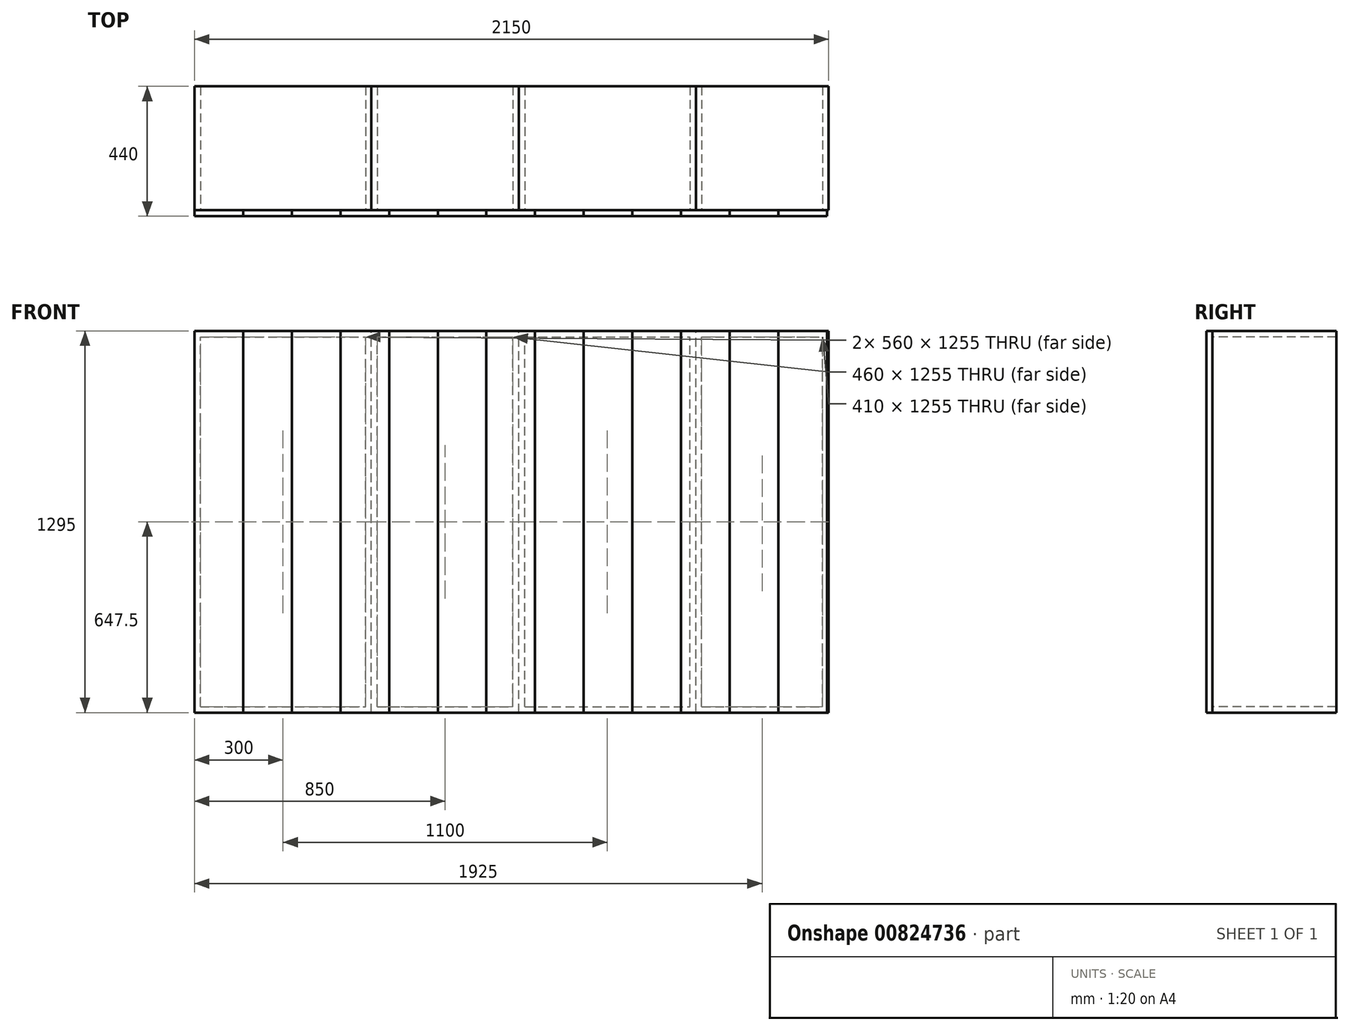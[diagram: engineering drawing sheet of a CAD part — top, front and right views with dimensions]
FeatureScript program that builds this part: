
annotation { "Feature Type Name" : "Feature", "Feature Type Description" : "" }
export const myFeature = defineFeature(function(context is Context, id is Id, definition is map)
    precondition{}
    {
        {
            var Q0;
            Q0=qCreatedBy(makeId("Front.planeOp"),FACE);
            var sketch = newSketch(context, id + "F0", { "sketchPlane" : qUnion([Q0])});
            skLineSegment(sketch, "E0.bottom", {"start": v(0, 0) * mm, "end": v(600, 0) * mm});
            skLineSegment(sketch, "E0.top", {"start": v(0, 1295) * mm, "end": v(600, 1295) * mm});
            skLineSegment(sketch, "E0.left", {"start": v(0, 0) * mm, "end": v(0, 1295) * mm});
            skLineSegment(sketch, "E0.right", {"start": v(600, 0) * mm, "end": v(600, 1295) * mm});
            skLineSegment(sketch, "E1.0", {"start": v(20, 1275) * mm, "end": v(580, 1275) * mm});
            skLineSegment(sketch, "E1.1", {"start": v(20, 20) * mm, "end": v(20, 1275) * mm});
            skLineSegment(sketch, "E1.2", {"start": v(20, 20) * mm, "end": v(580, 20) * mm});
            skLineSegment(sketch, "E1.3", {"start": v(580, 20) * mm, "end": v(580, 1275) * mm});
            skSolve(sketch);
        }
        {
            var Q0;
            Q0 = qSketchRegion(id + "F0", true);
            extrude(context, id + "F1", {"entities" : qUnion([Q0]), "oppositeDirection" : true, "depth" : 420 * mm, "offsetDistance" : 25 * mm});
        }
        {
            var Q0;
            Q0=makeQuery(id+"F1.opExtrude","CAP_FACE",FACE,{"disambiguationData":[OSD([sQuery(id+"F0.wireOp",EDGE,"E0.bottom"),sQuery(id+"F0.wireOp",EDGE,"E0.top"),sQuery(id+"F0.wireOp",EDGE,"E0.left"),sQuery(id+"F0.wireOp",EDGE,"E0.right"),sQuery(id+"F0.wireOp",EDGE,"E1.0"),sQuery(id+"F0.wireOp",EDGE,"E1.1"),sQuery(id+"F0.wireOp",EDGE,"E1.2"),sQuery(id+"F0.wireOp",EDGE,"E1.3")])],"isStart":true});
            var sketch = newSketch(context, id + "F2", { "sketchPlane" : qUnion([Q0])});
            skLineSegment(sketch, "E2.bottom", {"start": v(600, 0) * mm, "end": v(1100, 0) * mm});
            skLineSegment(sketch, "E2.top", {"start": v(600, 1295) * mm, "end": v(1100, 1295) * mm});
            skLineSegment(sketch, "E2.left", {"start": v(600, 0) * mm, "end": v(600, 1295) * mm});
            skLineSegment(sketch, "E2.right", {"start": v(1100, 0) * mm, "end": v(1100, 1295) * mm});
            skLineSegment(sketch, "E3.0", {"start": v(620, 20) * mm, "end": v(620, 1275) * mm});
            skLineSegment(sketch, "E3.1", {"start": v(620, 20) * mm, "end": v(1080, 20) * mm});
            skLineSegment(sketch, "E3.2", {"start": v(1080, 20) * mm, "end": v(1080, 1275) * mm});
            skLineSegment(sketch, "E3.3", {"start": v(620, 1275) * mm, "end": v(1080, 1275) * mm});
            skSolve(sketch);
        }
        {
            var Q0;
            Q0 = qSketchRegion(id + "F2", true);
            extrude(context, id + "F3", {"entities" : qUnion([Q0]), "oppositeDirection" : true, "depth" : 420 * mm, "offsetDistance" : 25 * mm});
        }
        {
            var Q0;
            Q0=makeQuery(id+"F3.opExtrude","CAP_FACE",FACE,{"disambiguationData":[OSD([sQuery(id+"F2.wireOp",EDGE,"E2.bottom"),sQuery(id+"F2.wireOp",EDGE,"E2.top"),sQuery(id+"F2.wireOp",EDGE,"E2.left"),sQuery(id+"F2.wireOp",EDGE,"E2.right"),sQuery(id+"F2.wireOp",EDGE,"E3.0"),sQuery(id+"F2.wireOp",EDGE,"E3.1"),sQuery(id+"F2.wireOp",EDGE,"E3.2"),sQuery(id+"F2.wireOp",EDGE,"E3.3")])],"isStart":true});
            var sketch = newSketch(context, id + "F4", { "sketchPlane" : qUnion([Q0])});
            skLineSegment(sketch, "E4.bottom", {"start": v(1100, 0) * mm, "end": v(1700, 0) * mm});
            skLineSegment(sketch, "E4.top", {"start": v(1100, 1295) * mm, "end": v(1700, 1295) * mm});
            skLineSegment(sketch, "E4.left", {"start": v(1100, 0) * mm, "end": v(1100, 1295) * mm});
            skLineSegment(sketch, "E4.right", {"start": v(1700, 0) * mm, "end": v(1700, 1295) * mm});
            skLineSegment(sketch, "E5.0", {"start": v(1120, 20) * mm, "end": v(1120, 1275) * mm});
            skLineSegment(sketch, "E5.1", {"start": v(1120, 20) * mm, "end": v(1680, 20) * mm});
            skLineSegment(sketch, "E5.2", {"start": v(1680, 20) * mm, "end": v(1680, 1275) * mm});
            skLineSegment(sketch, "E5.3", {"start": v(1120, 1275) * mm, "end": v(1680, 1275) * mm});
            skSolve(sketch);
        }
        {
            var Q0;
            Q0 = qSketchRegion(id + "F4", true);
            extrude(context, id + "F5", {"entities" : qUnion([Q0]), "oppositeDirection" : true, "depth" : 420 * mm, "offsetDistance" : 25 * mm});
        }
        {
            var Q0;
            Q0=makeQuery(id+"F5.opExtrude","CAP_FACE",FACE,{"disambiguationData":[OSD([sQuery(id+"F4.wireOp",EDGE,"E4.bottom"),sQuery(id+"F4.wireOp",EDGE,"E4.top"),sQuery(id+"F4.wireOp",EDGE,"E4.left"),sQuery(id+"F4.wireOp",EDGE,"E4.right"),sQuery(id+"F4.wireOp",EDGE,"E5.0"),sQuery(id+"F4.wireOp",EDGE,"E5.1"),sQuery(id+"F4.wireOp",EDGE,"E5.2"),sQuery(id+"F4.wireOp",EDGE,"E5.3")])],"isStart":true});
            var sketch = newSketch(context, id + "F6", { "sketchPlane" : qUnion([Q0])});
            skLineSegment(sketch, "E6.bottom", {"start": v(1700, 0) * mm, "end": v(2150, 0) * mm});
            skLineSegment(sketch, "E6.top", {"start": v(1700, 1295) * mm, "end": v(2150, 1295) * mm});
            skLineSegment(sketch, "E6.left", {"start": v(1700, 0) * mm, "end": v(1700, 1295) * mm});
            skLineSegment(sketch, "E6.right", {"start": v(2150, 0) * mm, "end": v(2150, 1295) * mm});
            skLineSegment(sketch, "E7.0", {"start": v(1720, 20) * mm, "end": v(1720, 1275) * mm});
            skLineSegment(sketch, "E7.1", {"start": v(1720, 20) * mm, "end": v(2130, 20) * mm});
            skLineSegment(sketch, "E7.2", {"start": v(2130, 20) * mm, "end": v(2130, 1275) * mm});
            skLineSegment(sketch, "E7.3", {"start": v(1720, 1275) * mm, "end": v(2130, 1275) * mm});
            skSolve(sketch);
        }
        {
            var Q0;
            Q0 = qSketchRegion(id + "F6", true);
            extrude(context, id + "F7", {"entities" : qUnion([Q0]), "oppositeDirection" : true, "depth" : 420 * mm, "offsetDistance" : 25 * mm});
        }
        {
            var Q0;
            Q0=makeQuery(id+"F1.opExtrude","CAP_FACE",FACE,{"disambiguationData":[OSD([sQuery(id+"F0.wireOp",EDGE,"E0.bottom"),sQuery(id+"F0.wireOp",EDGE,"E0.top"),sQuery(id+"F0.wireOp",EDGE,"E0.left"),sQuery(id+"F0.wireOp",EDGE,"E0.right"),sQuery(id+"F0.wireOp",EDGE,"E1.0"),sQuery(id+"F0.wireOp",EDGE,"E1.1"),sQuery(id+"F0.wireOp",EDGE,"E1.2"),sQuery(id+"F0.wireOp",EDGE,"E1.3")])],"isStart":true});
            var sketch = newSketch(context, id + "F8", { "sketchPlane" : qUnion([Q0])});
            skLineSegment(sketch, "E8.bottom", {"start": v(0, 0) * mm, "end": v(165, 0) * mm});
            skLineSegment(sketch, "E8.top", {"start": v(0, 1295) * mm, "end": v(165, 1295) * mm});
            skLineSegment(sketch, "E8.left", {"start": v(0, 0) * mm, "end": v(0, 1295) * mm});
            skLineSegment(sketch, "E8.right", {"start": v(165, 0) * mm, "end": v(165, 1295) * mm});
            skSolve(sketch);
        }
        {
            var Q0;
            Q0 = qSketchRegion(id + "F8", true);
            extrude(context, id + "F9", {"entities" : qUnion([Q0]), "depth" : 20 * mm, "offsetDistance" : 25 * mm});
        }
        {
            var Q0;
            Q0=makeQuery(id+"F9.opExtrude","CAP_FACE",FACE,{"disambiguationData":[OSD([sQuery(id+"F8.wireOp",EDGE,"E8.bottom"),sQuery(id+"F8.wireOp",EDGE,"E8.top"),sQuery(id+"F8.wireOp",EDGE,"E8.left"),sQuery(id+"F8.wireOp",EDGE,"E8.right")])],"isStart":false});
            var sketch = newSketch(context, id + "F10", { "sketchPlane" : qUnion([Q0])});
            skLineSegment(sketch, "E9.bottom", {"start": v(165, 0) * mm, "end": v(330, 0) * mm});
            skLineSegment(sketch, "E9.top", {"start": v(165, 1295) * mm, "end": v(330, 1295) * mm});
            skLineSegment(sketch, "E9.left", {"start": v(165, 0) * mm, "end": v(165, 1295) * mm});
            skLineSegment(sketch, "E9.right", {"start": v(330, 0) * mm, "end": v(330, 1295) * mm});
            skSolve(sketch);
        }
        {
            var Q0;
            Q0 = qSketchRegion(id + "F10", true);
            extrude(context, id + "F11", {"entities" : qUnion([Q0]), "oppositeDirection" : true, "depth" : 20 * mm, "offsetDistance" : 25 * mm});
        }
        {
            var Q0;
            Q0=makeQuery(id+"F11.opExtrude","CAP_FACE",FACE,{"disambiguationData":[OSD([sQuery(id+"F10.wireOp",EDGE,"E9.bottom"),sQuery(id+"F10.wireOp",EDGE,"E9.top"),sQuery(id+"F10.wireOp",EDGE,"E9.left"),sQuery(id+"F10.wireOp",EDGE,"E9.right")])],"isStart":true});
            var sketch = newSketch(context, id + "F12", { "sketchPlane" : qUnion([Q0])});
            skLineSegment(sketch, "E10.bottom", {"start": v(330, 0) * mm, "end": v(495, 0) * mm});
            skLineSegment(sketch, "E10.top", {"start": v(330, 1295) * mm, "end": v(495, 1295) * mm});
            skLineSegment(sketch, "E10.left", {"start": v(330, 0) * mm, "end": v(330, 1295) * mm});
            skLineSegment(sketch, "E10.right", {"start": v(495, 0) * mm, "end": v(495, 1295) * mm});
            skSolve(sketch);
        }
        {
            var Q0;
            Q0 = qSketchRegion(id + "F12", true);
            extrude(context, id + "F13", {"entities" : qUnion([Q0]), "oppositeDirection" : true, "depth" : 20 * mm, "offsetDistance" : 25 * mm});
        }
        {
            var Q0;
            Q0=makeQuery(id+"F13.opExtrude","CAP_FACE",FACE,{"disambiguationData":[OSD([sQuery(id+"F12.wireOp",EDGE,"E10.bottom"),sQuery(id+"F12.wireOp",EDGE,"E10.top"),sQuery(id+"F12.wireOp",EDGE,"E10.left"),sQuery(id+"F12.wireOp",EDGE,"E10.right")])],"isStart":true});
            var sketch = newSketch(context, id + "F14", { "sketchPlane" : qUnion([Q0])});
            skLineSegment(sketch, "E11.bottom", {"start": v(495, 0) * mm, "end": v(660, 0) * mm});
            skLineSegment(sketch, "E11.top", {"start": v(495, 1295) * mm, "end": v(660, 1295) * mm});
            skLineSegment(sketch, "E11.left", {"start": v(495, 0) * mm, "end": v(495, 1295) * mm});
            skLineSegment(sketch, "E11.right", {"start": v(660, 0) * mm, "end": v(660, 1295) * mm});
            skSolve(sketch);
        }
        {
            var Q0;
            Q0 = qSketchRegion(id + "F14", true);
            extrude(context, id + "F15", {"entities" : qUnion([Q0]), "oppositeDirection" : true, "depth" : 20 * mm, "offsetDistance" : 25 * mm});
        }
        {
            var Q0;
            Q0=makeQuery(id+"F15.opExtrude","CAP_FACE",FACE,{"disambiguationData":[OSD([sQuery(id+"F14.wireOp",EDGE,"E11.bottom"),sQuery(id+"F14.wireOp",EDGE,"E11.top"),sQuery(id+"F14.wireOp",EDGE,"E11.left"),sQuery(id+"F14.wireOp",EDGE,"E11.right")])],"isStart":true});
            var sketch = newSketch(context, id + "F16", { "sketchPlane" : qUnion([Q0])});
            skLineSegment(sketch, "E12.bottom", {"start": v(660, 0) * mm, "end": v(825, 0) * mm});
            skLineSegment(sketch, "E12.top", {"start": v(660, 1295) * mm, "end": v(825, 1295) * mm});
            skLineSegment(sketch, "E12.left", {"start": v(660, 0) * mm, "end": v(660, 1295) * mm});
            skLineSegment(sketch, "E12.right", {"start": v(825, 0) * mm, "end": v(825, 1295) * mm});
            skSolve(sketch);
        }
        {
            var Q0;
            Q0 = qSketchRegion(id + "F16", true);
            extrude(context, id + "F17", {"entities" : qUnion([Q0]), "oppositeDirection" : true, "depth" : 20 * mm, "offsetDistance" : 25 * mm});
        }
        {
            var Q0;
            Q0=makeQuery(id+"F17.opExtrude","CAP_FACE",FACE,{"disambiguationData":[OSD([sQuery(id+"F16.wireOp",EDGE,"E12.bottom"),sQuery(id+"F16.wireOp",EDGE,"E12.top"),sQuery(id+"F16.wireOp",EDGE,"E12.left"),sQuery(id+"F16.wireOp",EDGE,"E12.right")])],"isStart":true});
            var sketch = newSketch(context, id + "F18", { "sketchPlane" : qUnion([Q0])});
            skLineSegment(sketch, "E13.bottom", {"start": v(825, 0) * mm, "end": v(990, 0) * mm});
            skLineSegment(sketch, "E13.top", {"start": v(825, 1295) * mm, "end": v(990, 1295) * mm});
            skLineSegment(sketch, "E13.left", {"start": v(825, 0) * mm, "end": v(825, 1295) * mm});
            skLineSegment(sketch, "E13.right", {"start": v(990, 0) * mm, "end": v(990, 1295) * mm});
            skSolve(sketch);
        }
        {
            var Q0;
            Q0 = qSketchRegion(id + "F18", true);
            extrude(context, id + "F19", {"entities" : qUnion([Q0]), "oppositeDirection" : true, "depth" : 20 * mm, "offsetDistance" : 25 * mm});
        }
        {
            var Q0;
            Q0=makeQuery(id+"F19.opExtrude","CAP_FACE",FACE,{"disambiguationData":[OSD([sQuery(id+"F18.wireOp",EDGE,"E13.bottom"),sQuery(id+"F18.wireOp",EDGE,"E13.top"),sQuery(id+"F18.wireOp",EDGE,"E13.left"),sQuery(id+"F18.wireOp",EDGE,"E13.right")])],"isStart":true});
            var sketch = newSketch(context, id + "F20", { "sketchPlane" : qUnion([Q0])});
            skLineSegment(sketch, "E14.bottom", {"start": v(990, 0) * mm, "end": v(1155, 0) * mm});
            skLineSegment(sketch, "E14.top", {"start": v(990, 1295) * mm, "end": v(1155, 1295) * mm});
            skLineSegment(sketch, "E14.left", {"start": v(990, 0) * mm, "end": v(990, 1295) * mm});
            skLineSegment(sketch, "E14.right", {"start": v(1155, 0) * mm, "end": v(1155, 1295) * mm});
            skSolve(sketch);
        }
        {
            var Q0;
            Q0 = qSketchRegion(id + "F20", true);
            extrude(context, id + "F21", {"entities" : qUnion([Q0]), "oppositeDirection" : true, "depth" : 20 * mm, "offsetDistance" : 25 * mm});
        }
        {
            var Q0;
            Q0=makeQuery(id+"F21.opExtrude","CAP_FACE",FACE,{"disambiguationData":[OSD([sQuery(id+"F20.wireOp",EDGE,"E14.bottom"),sQuery(id+"F20.wireOp",EDGE,"E14.top"),sQuery(id+"F20.wireOp",EDGE,"E14.left"),sQuery(id+"F20.wireOp",EDGE,"E14.right")])],"isStart":true});
            var sketch = newSketch(context, id + "F22", { "sketchPlane" : qUnion([Q0])});
            skLineSegment(sketch, "E15.bottom", {"start": v(1155, 0) * mm, "end": v(1320, 0) * mm});
            skLineSegment(sketch, "E15.top", {"start": v(1155, 1295) * mm, "end": v(1320, 1295) * mm});
            skLineSegment(sketch, "E15.left", {"start": v(1155, 0) * mm, "end": v(1155, 1295) * mm});
            skLineSegment(sketch, "E15.right", {"start": v(1320, 0) * mm, "end": v(1320, 1295) * mm});
            skSolve(sketch);
        }
        {
            var Q0;
            Q0 = qSketchRegion(id + "F22", true);
            extrude(context, id + "F23", {"entities" : qUnion([Q0]), "oppositeDirection" : true, "depth" : 20 * mm, "offsetDistance" : 25 * mm});
        }
        {
            var Q0;
            Q0=makeQuery(id+"F23.opExtrude","CAP_FACE",FACE,{"disambiguationData":[OSD([sQuery(id+"F22.wireOp",EDGE,"E15.bottom"),sQuery(id+"F22.wireOp",EDGE,"E15.top"),sQuery(id+"F22.wireOp",EDGE,"E15.left"),sQuery(id+"F22.wireOp",EDGE,"E15.right")])],"isStart":true});
            var sketch = newSketch(context, id + "F24", { "sketchPlane" : qUnion([Q0])});
            skLineSegment(sketch, "E16.bottom", {"start": v(1320, 0) * mm, "end": v(1485, 0) * mm});
            skLineSegment(sketch, "E16.top", {"start": v(1320, 1295) * mm, "end": v(1485, 1295) * mm});
            skLineSegment(sketch, "E16.left", {"start": v(1320, 0) * mm, "end": v(1320, 1295) * mm});
            skLineSegment(sketch, "E16.right", {"start": v(1485, 0) * mm, "end": v(1485, 1295) * mm});
            skSolve(sketch);
        }
        {
            var Q0;
            Q0 = qSketchRegion(id + "F24", true);
            extrude(context, id + "F25", {"entities" : qUnion([Q0]), "oppositeDirection" : true, "depth" : 20 * mm, "offsetDistance" : 25 * mm});
        }
        {
            var Q0;
            Q0=makeQuery(id+"F25.opExtrude","CAP_FACE",FACE,{"disambiguationData":[OSD([sQuery(id+"F24.wireOp",EDGE,"E16.bottom"),sQuery(id+"F24.wireOp",EDGE,"E16.top"),sQuery(id+"F24.wireOp",EDGE,"E16.left"),sQuery(id+"F24.wireOp",EDGE,"E16.right")])],"isStart":true});
            var sketch = newSketch(context, id + "F26", { "sketchPlane" : qUnion([Q0])});
            skLineSegment(sketch, "E17.bottom", {"start": v(1485, 0) * mm, "end": v(1650, 0) * mm});
            skLineSegment(sketch, "E17.top", {"start": v(1485, 1295) * mm, "end": v(1650, 1295) * mm});
            skLineSegment(sketch, "E17.left", {"start": v(1485, 0) * mm, "end": v(1485, 1295) * mm});
            skLineSegment(sketch, "E17.right", {"start": v(1650, 0) * mm, "end": v(1650, 1295) * mm});
            skSolve(sketch);
        }
        {
            var Q0;
            Q0 = qSketchRegion(id + "F26", true);
            extrude(context, id + "F27", {"entities" : qUnion([Q0]), "oppositeDirection" : true, "depth" : 20 * mm, "offsetDistance" : 25 * mm});
        }
        {
            var Q0;
            Q0=makeQuery(id+"F27.opExtrude","CAP_FACE",FACE,{"disambiguationData":[OSD([sQuery(id+"F26.wireOp",EDGE,"E17.bottom"),sQuery(id+"F26.wireOp",EDGE,"E17.top"),sQuery(id+"F26.wireOp",EDGE,"E17.left"),sQuery(id+"F26.wireOp",EDGE,"E17.right")])],"isStart":true});
            var sketch = newSketch(context, id + "F28", { "sketchPlane" : qUnion([Q0])});
            skLineSegment(sketch, "E18.bottom", {"start": v(1650, 0) * mm, "end": v(1815, 0) * mm});
            skLineSegment(sketch, "E18.top", {"start": v(1650, 1295) * mm, "end": v(1815, 1295) * mm});
            skLineSegment(sketch, "E18.left", {"start": v(1650, 0) * mm, "end": v(1650, 1295) * mm});
            skLineSegment(sketch, "E18.right", {"start": v(1815, 0) * mm, "end": v(1815, 1295) * mm});
            skSolve(sketch);
        }
        {
            var Q0;
            Q0 = qSketchRegion(id + "F28", true);
            extrude(context, id + "F29", {"entities" : qUnion([Q0]), "oppositeDirection" : true, "depth" : 20 * mm, "offsetDistance" : 25 * mm});
        }
        {
            var Q0;
            Q0=makeQuery(id+"F29.opExtrude","CAP_FACE",FACE,{"disambiguationData":[OSD([sQuery(id+"F28.wireOp",EDGE,"E18.bottom"),sQuery(id+"F28.wireOp",EDGE,"E18.top"),sQuery(id+"F28.wireOp",EDGE,"E18.left"),sQuery(id+"F28.wireOp",EDGE,"E18.right")])],"isStart":true});
            var sketch = newSketch(context, id + "F30", { "sketchPlane" : qUnion([Q0])});
            skLineSegment(sketch, "E19.bottom", {"start": v(1815, 0) * mm, "end": v(1980, 0) * mm});
            skLineSegment(sketch, "E19.top", {"start": v(1815, 1295) * mm, "end": v(1980, 1295) * mm});
            skLineSegment(sketch, "E19.left", {"start": v(1815, 0) * mm, "end": v(1815, 1295) * mm});
            skLineSegment(sketch, "E19.right", {"start": v(1980, 0) * mm, "end": v(1980, 1295) * mm});
            skSolve(sketch);
        }
        {
            var Q0;
            Q0 = qSketchRegion(id + "F30", true);
            extrude(context, id + "F31", {"entities" : qUnion([Q0]), "oppositeDirection" : true, "depth" : 20 * mm, "offsetDistance" : 25 * mm});
        }
        {
            var Q0;
            Q0=makeQuery(id+"F31.opExtrude","CAP_FACE",FACE,{"disambiguationData":[OSD([sQuery(id+"F30.wireOp",EDGE,"E19.bottom"),sQuery(id+"F30.wireOp",EDGE,"E19.top"),sQuery(id+"F30.wireOp",EDGE,"E19.left"),sQuery(id+"F30.wireOp",EDGE,"E19.right")])],"isStart":true});
            var sketch = newSketch(context, id + "F32", { "sketchPlane" : qUnion([Q0])});
            skLineSegment(sketch, "E20.bottom", {"start": v(1980, 0) * mm, "end": v(2145, 0) * mm});
            skLineSegment(sketch, "E20.top", {"start": v(1980, 1295) * mm, "end": v(2145, 1295) * mm});
            skLineSegment(sketch, "E20.left", {"start": v(1980, 0) * mm, "end": v(1980, 1295) * mm});
            skLineSegment(sketch, "E20.right", {"start": v(2145, 0) * mm, "end": v(2145, 1295) * mm});
            skSolve(sketch);
        }
        {
            var Q0;
            Q0 = qSketchRegion(id + "F32", true);
            extrude(context, id + "F33", {"entities" : qUnion([Q0]), "oppositeDirection" : true, "depth" : 20 * mm, "offsetDistance" : 25 * mm});
        }
    });
